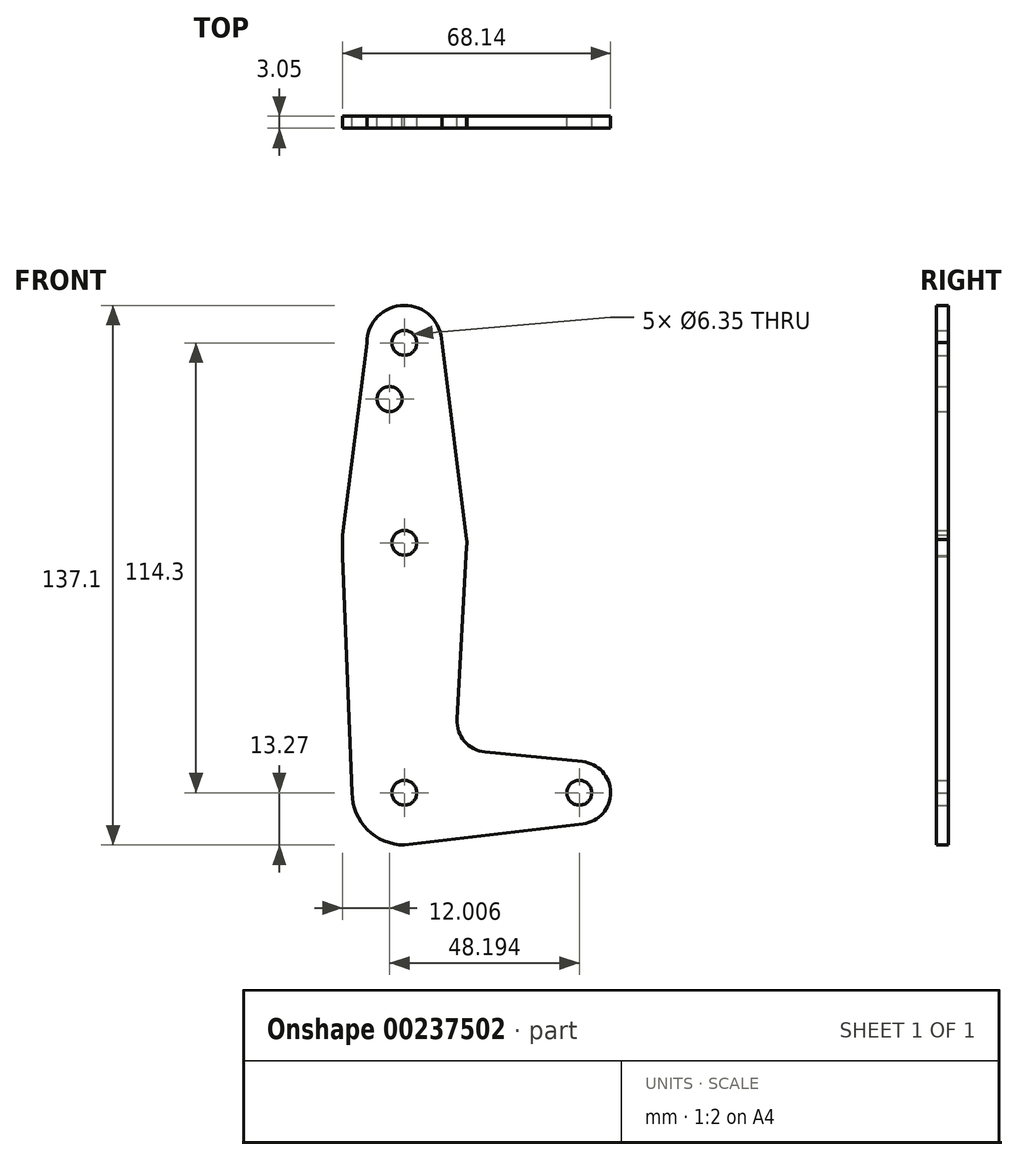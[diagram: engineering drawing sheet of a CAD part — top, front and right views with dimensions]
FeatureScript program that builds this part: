
annotation { "Feature Type Name" : "Feature", "Feature Type Description" : "" }
export const myFeature = defineFeature(function(context is Context, id is Id, definition is map)
    precondition{}
    {
        {
            var Q0;
            Q0=qCreatedBy(makeId("Front.planeOp"),FACE);
            var sketch = newSketch(context, id + "F0", { "sketchPlane" : qUnion([Q0])});
            skCircle(sketch, "E0", {"center": v(0, 0) * mm, "radius": 13.27 * mm});
            skCircle(sketch, "E1", {"center": v(0, 63.5) * mm, "radius": 15.88 * mm});
            skCircle(sketch, "E2", {"center": v(0, 114.3) * mm, "radius": 9.53 * mm});
            skCircle(sketch, "E3", {"center": v(44.45, 0) * mm, "radius": 7.94 * mm});
            skLineSegment(sketch, "E4", {"start": v(0, 0) * mm, "end": v(44.45, 0) * mm, "construction": true});
            skLineSegment(sketch, "E5", {"start": v(0, 0) * mm, "end": v(0, 114.3) * mm, "construction": true});
            skLineSegment(sketch, "E6", {"start": v(0, 63.5) * mm, "end": v(0, 0) * mm, "construction": true});
            skLineSegment(sketch, "E7", {"start": v(20.55, 10.32) * mm, "end": v(45.23, 7.9) * mm});
            skLineSegment(sketch, "E8", {"start": v(0, -13.27) * mm, "end": v(45.39, -7.88) * mm});
            skLineSegment(sketch, "E9", {"start": v(13.4, 18.68) * mm, "end": v(15.85, 62.61) * mm});
            skLineSegment(sketch, "E10", {"start": v(9.52, 114.41) * mm, "end": v(15.85, 64.39) * mm});
            skCircle(sketch, "E11", {"center": v(0, 114.3) * mm, "radius": 3.18 * mm});
            skCircle(sketch, "E12", {"center": v(0, 63.5) * mm, "radius": 3.18 * mm});
            skCircle(sketch, "E13", {"center": v(0, 0) * mm, "radius": 3.18 * mm});
            skCircle(sketch, "E14", {"center": v(44.45, 0) * mm, "radius": 3.18 * mm});
            skCircle(sketch, "E15", {"center": v(-3.74, 100.03) * mm, "radius": 3.18 * mm});
            skLineSegment(sketch, "E16", {"start": v(0, 100.03) * mm, "end": v(0, 63.5) * mm, "construction": true});
            skArc(sketch, "E17.filletArc", {"start": v(13.4, 18.68) * mm, "mid": v(15.3, 13.06) * mm, "end": v(20.55, 10.32) * mm});
            skLineSegment(sketch, "E18", {"start": v(-9.53, 114.3) * mm, "end": v(-15.75, 65.5) * mm});
            skLineSegment(sketch, "E19", {"start": v(-13.27, 0) * mm, "end": v(-15.75, 60.08) * mm});
            skLineSegment(sketch, "E20", {"start": v(-15.75, 60.08) * mm, "end": v(-15.75, 65.5) * mm});
            skSolve(sketch);
        }
        {
            var Q0;
            Q0=makeQuery(id+"F0.imprint","IMPRINT",FACE,{"disambiguationData":[TD([[makeQuery(id+"F0.imprint","IMPRINT",EDGE,{"derivedFrom":sQuery(id+"F0.wireOp",EDGE,"E15")}),-1.0]])]});
            var Q1;
            {var subQ0=sQuery(id+"F0.wireOp",EDGE,"E10");var subQ3=sQuery(id+"F0.wireOp",EDGE,"E1");var subQ4=makeQuery(id+"F0.imprint","INTERSECT",VERTEX,{"disambiguationData":[OD(1.0)],"derivedFrom":[subQ3,subQ0]});Q1=makeQuery(id+"F0.imprint","IMPRINT",FACE,{"disambiguationData":[TD([[makeQuery(id+"F0.imprint","IMPRINT",EDGE,{"disambiguationData":[TD([[subQ4,-1.0]])],"derivedFrom":subQ3}),-1.0]])]});}
            var Q2;
            Q2=makeQuery(id+"F0.imprint","IMPRINT",FACE,{"disambiguationData":[TD([[makeQuery(id+"F0.imprint","IMPRINT",EDGE,{"derivedFrom":sQuery(id+"F0.wireOp",EDGE,"E11")}),-1.0]])]});
            var Q3;
            {var subQ1=sQuery(id+"F0.wireOp",EDGE,"E1");var subQ6=sQuery(id+"F0.wireOp",EDGE,"E10");var subQ11=makeQuery(id+"F0.imprint","INTERSECT",VERTEX,{"disambiguationData":[OD(1.0)],"derivedFrom":[subQ1,subQ6]});Q3=makeQuery(id+"F0.imprint","IMPRINT",FACE,{"disambiguationData":[TD([[makeQuery(id+"F0.imprint","IMPRINT",EDGE,{"disambiguationData":[TD([[subQ11,-1.0]])],"derivedFrom":subQ1}),1.0]])]});}
            var Q4;
            {var subQ1=sQuery(id+"F0.wireOp",EDGE,"E1");var subQ5=sQuery(id+"F0.wireOp",EDGE,"E20");var subQ6=makeQuery(id+"F0.imprint","INTERSECT",VERTEX,{"derivedFrom":[subQ1,subQ5]});Q4=makeQuery(id+"F0.imprint","IMPRINT",FACE,{"disambiguationData":[TD([[makeQuery(id+"F0.imprint","IMPRINT",EDGE,{"disambiguationData":[TD([[subQ6,-1.0]])],"derivedFrom":subQ1}),1.0]])]});}
            var Q5;
            {var subQ0=sQuery(id+"F0.wireOp",EDGE,"E19");Q5=makeQuery(id+"F0.imprint","IMPRINT",FACE,{"disambiguationData":[TD([[makeQuery(id+"F0.imprint","IMPRINT",EDGE,{"derivedFrom":subQ0}),-1.0]])]});}
            var Q6;
            {var subQ7=sQuery(id+"F0.wireOp",EDGE,"E7");Q6=makeQuery(id+"F0.imprint","IMPRINT",FACE,{"disambiguationData":[TD([[makeQuery(id+"F0.imprint","IMPRINT",EDGE,{"derivedFrom":subQ7}),-1.0]])]});}
            var Q7;
            {var subQ0=sQuery(id+"F0.wireOp",EDGE,"E8");var subQ1=sQuery(id+"F0.wireOp",EDGE,"E0");var subQ2=makeQuery(id+"F0.imprint","INTERSECT",VERTEX,{"disambiguationData":[OD(1.0)],"derivedFrom":[subQ1,subQ0]});Q7=makeQuery(id+"F0.imprint","IMPRINT",FACE,{"disambiguationData":[TD([[makeQuery(id+"F0.imprint","IMPRINT",EDGE,{"disambiguationData":[TD([[subQ2,-1.0]])],"derivedFrom":subQ1}),-1.0]])]});}
            var Q8;
            Q8=makeQuery(id+"F0.imprint","IMPRINT",FACE,{"disambiguationData":[TD([[makeQuery(id+"F0.imprint","IMPRINT",EDGE,{"derivedFrom":sQuery(id+"F0.wireOp",EDGE,"E14")}),-1.0]])]});
            var Q9;
            {var subQ1=sQuery(id+"F0.wireOp",EDGE,"E0");var subQ8=makeQuery(id+"F0.imprint","INTERSECT",VERTEX,{"derivedFrom":[subQ1,sQuery(id+"F0.wireOp",EDGE,"E19")]});Q9=makeQuery(id+"F0.imprint","IMPRINT",FACE,{"disambiguationData":[TD([[makeQuery(id+"F0.imprint","IMPRINT",EDGE,{"disambiguationData":[TD([[subQ8,1.0]])],"derivedFrom":subQ1}),1.0]])]});}
            var Q10;
            {var subQ0=sQuery(id+"F0.wireOp",EDGE,"E6");var subQ1=sQuery(id+"F0.wireOp",EDGE,"E0");var subQ2=makeQuery(id+"F0.imprint","INTERSECT",VERTEX,{"derivedFrom":[subQ1,subQ0]});Q10=makeQuery(id+"F0.imprint","IMPRINT",FACE,{"disambiguationData":[TD([[makeQuery(id+"F0.imprint","IMPRINT",EDGE,{"disambiguationData":[TD([[subQ2,1.0]])],"derivedFrom":subQ1}),1.0]])]});}
            extrude(context, id + "F1", {"entities" : qUnion([Q0, Q1, Q2, Q3, Q4, Q5, Q6, Q7, Q8, Q9, Q10]), "depth" : 3.05 * mm});
        }
    });
